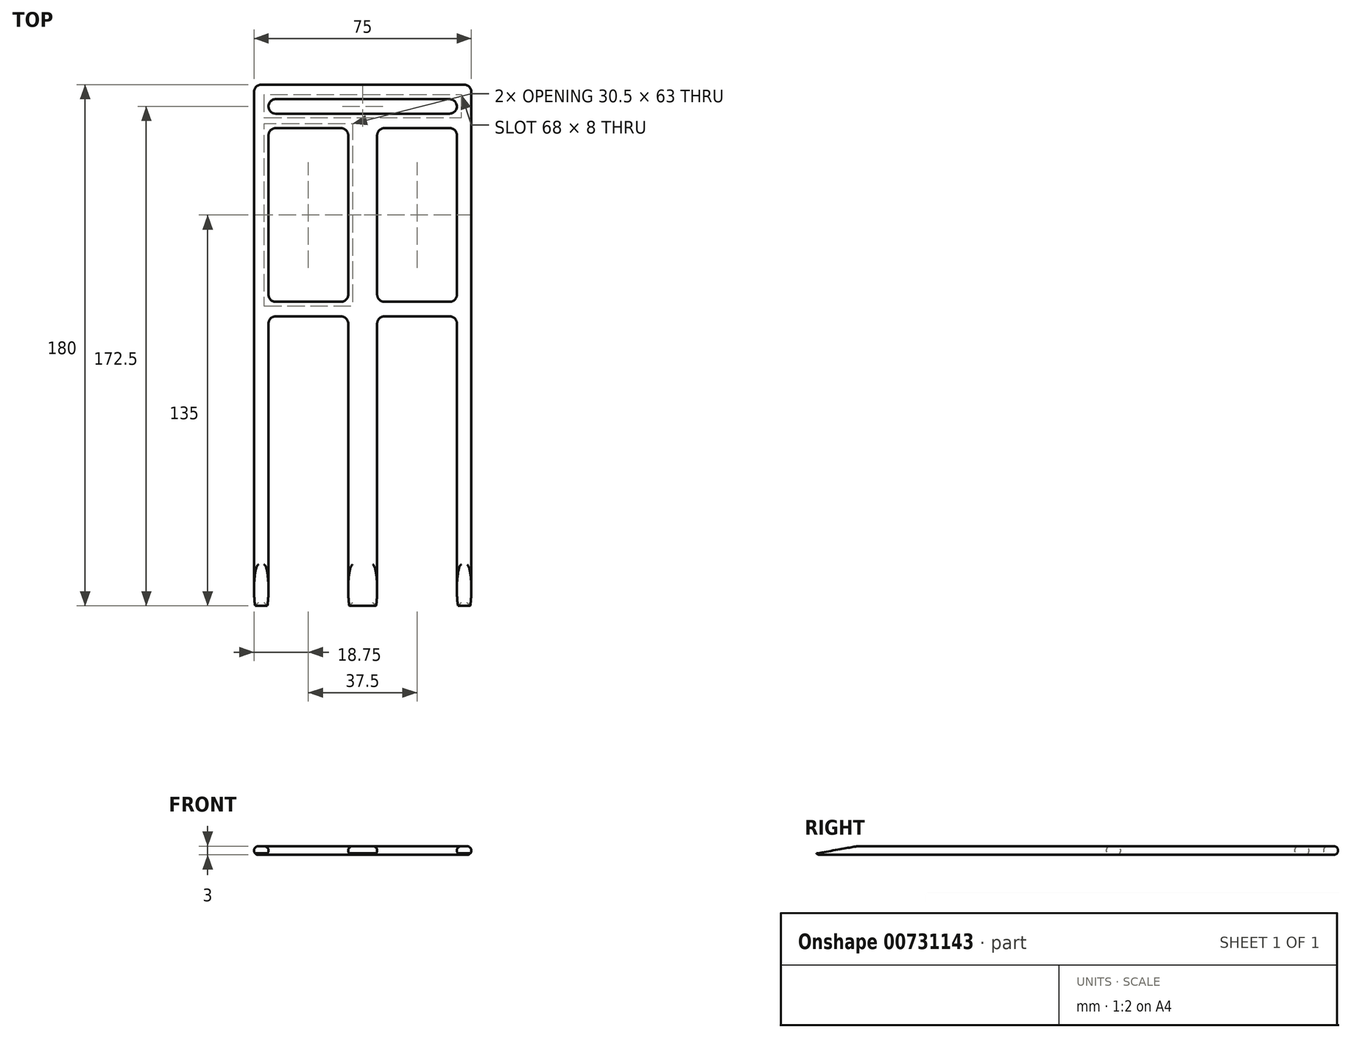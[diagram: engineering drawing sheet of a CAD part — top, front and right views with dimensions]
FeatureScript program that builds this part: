
annotation { "Feature Type Name" : "Feature", "Feature Type Description" : "" }
export const myFeature = defineFeature(function(context is Context, id is Id, definition is map)
    precondition{}
    {
        {
            var Q0;
            Q0=qCreatedBy(makeId("Top.planeOp"),FACE);
            var sketch = newSketch(context, id + "F0", { "sketchPlane" : qUnion([Q0])});
            skLineSegment(sketch, "E0.bottom", {"start": v(35, 90) * mm, "end": v(-35, 90) * mm});
            skLineSegment(sketch, "E0.top", {"start": v(37.5, -90) * mm, "end": v(32.5, -90) * mm});
            skLineSegment(sketch, "E0.left", {"start": v(37.5, 87.5) * mm, "end": v(37.5, -90) * mm});
            skLineSegment(sketch, "E0.right", {"start": v(-37.5, 87.5) * mm, "end": v(-37.5, -90) * mm});
            skPoint(sketch, "E0.middle", {"position": v(0, 0) * mm});
            skLineSegment(sketch, "E1", {"start": v(0, 0) * mm, "end": v(0, -90) * mm, "construction": true});
            skLineSegment(sketch, "E2", {"start": v(0, 0) * mm, "end": v(0, 90) * mm, "construction": true});
            skLineSegment(sketch, "E3", {"start": v(0, -45) * mm, "end": v(-18.75, -45) * mm, "construction": true});
            skLineSegment(sketch, "E4", {"start": v(0, -45) * mm, "end": v(18.75, -45) * mm, "construction": true});
            skLineSegment(sketch, "E5", {"start": v(0, 45) * mm, "end": v(-18.75, 45) * mm, "construction": true});
            skLineSegment(sketch, "E6", {"start": v(0, 45) * mm, "end": v(18.75, 45) * mm, "construction": true});
            skLineSegment(sketch, "E7.bottom", {"start": v(-7.5, 15) * mm, "end": v(-30, 15) * mm});
            skLineSegment(sketch, "E7.top", {"start": v(-7.5, 75) * mm, "end": v(-30, 75) * mm});
            skLineSegment(sketch, "E7.left", {"start": v(-5, 17.5) * mm, "end": v(-5, 72.5) * mm});
            skLineSegment(sketch, "E7.right", {"start": v(-32.5, 17.5) * mm, "end": v(-32.5, 72.5) * mm});
            skPoint(sketch, "E7.middle", {"position": v(-18.75, 45) * mm});
            skLineSegment(sketch, "E8.bottom", {"start": v(30, 15) * mm, "end": v(7.5, 15) * mm});
            skLineSegment(sketch, "E8.top", {"start": v(30, 75) * mm, "end": v(7.5, 75) * mm});
            skLineSegment(sketch, "E8.left", {"start": v(32.5, 17.5) * mm, "end": v(32.5, 72.5) * mm});
            skLineSegment(sketch, "E8.right", {"start": v(5, 17.5) * mm, "end": v(5, 72.5) * mm});
            skPoint(sketch, "E8.middle", {"position": v(18.75, 45) * mm});
            skLineSegment(sketch, "E9.top", {"start": v(-7.5, 10) * mm, "end": v(-30, 10) * mm});
            skLineSegment(sketch, "E9.left", {"start": v(-5, -90) * mm, "end": v(-5, 7.5) * mm});
            skLineSegment(sketch, "E9.right", {"start": v(-32.5, -90) * mm, "end": v(-32.5, 7.5) * mm});
            skPoint(sketch, "E9.middle", {"position": v(-18.75, -45) * mm});
            skLineSegment(sketch, "E10.top", {"start": v(30, 10) * mm, "end": v(7.5, 10) * mm});
            skLineSegment(sketch, "E10.left", {"start": v(32.5, -90) * mm, "end": v(32.5, 7.5) * mm});
            skLineSegment(sketch, "E10.right", {"start": v(5, -90) * mm, "end": v(5, 7.5) * mm});
            skPoint(sketch, "E10.middle", {"position": v(18.75, -45) * mm});
            skLineSegment(sketch, "E11", {"start": v(-18.75, 75) * mm, "end": v(-18.75, 90) * mm, "construction": true});
            skLineSegment(sketch, "E12", {"start": v(18.75, 75) * mm, "end": v(18.75, 90) * mm, "construction": true});
            skLineSegment(sketch, "E13", {"start": v(-18.75, 82.5) * mm, "end": v(18.75, 82.5) * mm, "construction": true});
            skPoint(sketch, "E14", {"position": v(0, 82.5) * mm});
            skLineSegment(sketch, "E15.bottom", {"start": v(30, 80) * mm, "end": v(-30, 80) * mm});
            skLineSegment(sketch, "E15.top", {"start": v(30, 85) * mm, "end": v(-30, 85) * mm});
            skLineSegment(sketch, "E15.left", {"start": v(32.5, 82.5) * mm, "end": v(32.5, 82.5) * mm});
            skLineSegment(sketch, "E15.right", {"start": v(-32.5, 82.5) * mm, "end": v(-32.5, 82.5) * mm});
            skLineSegment(sketch, "E16.trimOffspring", {"start": v(-32.5, -90) * mm, "end": v(-37.5, -90) * mm});
            skPoint(sketch, "E17.orphan", {"position": v(-32.5, -100) * mm});
            skPoint(sketch, "E18.orphan", {"position": v(-5, -100) * mm});
            skLineSegment(sketch, "E19.trimOffspring", {"start": v(5, -90) * mm, "end": v(-5, -90) * mm});
            skPoint(sketch, "E10.bottom.end.orphan", {"position": v(5, -100) * mm});
            skPoint(sketch, "E20.orphan", {"position": v(32.5, -100) * mm});
            skPoint(sketch, "E21.visualSharp", {"position": v(-37.5, 90) * mm});
            skArc(sketch, "E21.filletArc", {"start": v(-35, 90) * mm, "mid": v(-36.77, 89.27) * mm, "end": v(-37.5, 87.5) * mm});
            skPoint(sketch, "E22.visualSharp", {"position": v(37.5, 90) * mm});
            skArc(sketch, "E22.filletArc", {"start": v(37.5, 87.5) * mm, "mid": v(36.77, 89.27) * mm, "end": v(35, 90) * mm});
            skPoint(sketch, "E23.visualSharp", {"position": v(-32.5, 10) * mm});
            skArc(sketch, "E23.filletArc", {"start": v(-30, 10) * mm, "mid": v(-31.77, 9.27) * mm, "end": v(-32.5, 7.5) * mm});
            skPoint(sketch, "E24.visualSharp", {"position": v(-5, 10) * mm});
            skArc(sketch, "E24.filletArc", {"start": v(-5, 7.5) * mm, "mid": v(-5.73, 9.27) * mm, "end": v(-7.5, 10) * mm});
            skPoint(sketch, "E25.visualSharp", {"position": v(5, 10) * mm});
            skArc(sketch, "E25.filletArc", {"start": v(7.5, 10) * mm, "mid": v(5.73, 9.27) * mm, "end": v(5, 7.5) * mm});
            skPoint(sketch, "E26.visualSharp", {"position": v(32.5, 10) * mm});
            skArc(sketch, "E26.filletArc", {"start": v(32.5, 7.5) * mm, "mid": v(31.77, 9.27) * mm, "end": v(30, 10) * mm});
            skPoint(sketch, "E27.visualSharp", {"position": v(32.5, 15) * mm});
            skArc(sketch, "E27.filletArc", {"start": v(30, 15) * mm, "mid": v(31.77, 15.73) * mm, "end": v(32.5, 17.5) * mm});
            skPoint(sketch, "E28.visualSharp", {"position": v(5, 15) * mm});
            skArc(sketch, "E28.filletArc", {"start": v(5, 17.5) * mm, "mid": v(5.73, 15.73) * mm, "end": v(7.5, 15) * mm});
            skPoint(sketch, "E29.visualSharp", {"position": v(-5, 15) * mm});
            skArc(sketch, "E29.filletArc", {"start": v(-7.5, 15) * mm, "mid": v(-5.73, 15.73) * mm, "end": v(-5, 17.5) * mm});
            skPoint(sketch, "E30.visualSharp", {"position": v(-32.5, 15) * mm});
            skArc(sketch, "E30.filletArc", {"start": v(-32.5, 17.5) * mm, "mid": v(-31.77, 15.73) * mm, "end": v(-30, 15) * mm});
            skPoint(sketch, "E31.visualSharp", {"position": v(-32.5, 75) * mm});
            skArc(sketch, "E31.filletArc", {"start": v(-30, 75) * mm, "mid": v(-31.77, 74.27) * mm, "end": v(-32.5, 72.5) * mm});
            skPoint(sketch, "E32.visualSharp", {"position": v(-5, 75) * mm});
            skArc(sketch, "E32.filletArc", {"start": v(-5, 72.5) * mm, "mid": v(-5.73, 74.27) * mm, "end": v(-7.5, 75) * mm});
            skPoint(sketch, "E33.visualSharp", {"position": v(5, 75) * mm});
            skArc(sketch, "E33.filletArc", {"start": v(7.5, 75) * mm, "mid": v(5.73, 74.27) * mm, "end": v(5, 72.5) * mm});
            skPoint(sketch, "E34.visualSharp", {"position": v(32.5, 75) * mm});
            skArc(sketch, "E34.filletArc", {"start": v(32.5, 72.5) * mm, "mid": v(31.77, 74.27) * mm, "end": v(30, 75) * mm});
            skPoint(sketch, "E35.visualSharp", {"position": v(-32.5, 85) * mm});
            skArc(sketch, "E35.filletArc", {"start": v(-30, 85) * mm, "mid": v(-31.77, 84.27) * mm, "end": v(-32.5, 82.5) * mm});
            skPoint(sketch, "E36.visualSharp", {"position": v(-32.5, 80) * mm});
            skArc(sketch, "E36.filletArc", {"start": v(-32.5, 82.5) * mm, "mid": v(-31.77, 80.73) * mm, "end": v(-30, 80) * mm});
            skPoint(sketch, "E37.visualSharp", {"position": v(32.5, 80) * mm});
            skArc(sketch, "E37.filletArc", {"start": v(30, 80) * mm, "mid": v(31.77, 80.73) * mm, "end": v(32.5, 82.5) * mm});
            skPoint(sketch, "E38.visualSharp", {"position": v(32.5, 85) * mm});
            skArc(sketch, "E38.filletArc", {"start": v(32.5, 82.5) * mm, "mid": v(31.77, 84.27) * mm, "end": v(30, 85) * mm});
            skSolve(sketch);
        }
        {
            var Q0;
            Q0 = qSketchRegion(id + "F0", true);
            extrude(context, id + "F1", {"entities" : qUnion([Q0]), "depth" : 3 * mm, "offsetDistance" : 25 * mm});
        }
        {
            var Q0;
            Q0=makeQuery(id+"F1.opExtrude","CAP_EDGE",EDGE,{"disambiguationData":[OSD([sQuery(id+"F0.wireOp",EDGE,"E19.trimOffspring")])],"isStart":false});
            var Q1;
            Q1=makeQuery(id+"F1.opExtrude","CAP_EDGE",EDGE,{"disambiguationData":[OSD([sQuery(id+"F0.wireOp",EDGE,"E0.top")])],"isStart":false});
            var Q2;
            Q2=makeQuery(id+"F1.opExtrude","CAP_EDGE",EDGE,{"disambiguationData":[OSD([sQuery(id+"F0.wireOp",EDGE,"E16.trimOffspring")])],"isStart":false});
            chamfer(context, id + "F2", {"entities" : qUnion([Q0, Q1, Q2]), "chamferType" : ChamferType.OFFSET_ANGLE, "width" : 2.5 * mm, "oppositeDirection" : false, "angle" : 80 * degree});
        }
        {
            var Q0;
            Q0=makeQuery(id+"F1.opExtrude","CAP_FACE",FACE,{"disambiguationData":[OSD([sQuery(id+"F0.wireOp",EDGE,"E0.bottom"),sQuery(id+"F0.wireOp",EDGE,"E0.top"),sQuery(id+"F0.wireOp",EDGE,"E0.left"),sQuery(id+"F0.wireOp",EDGE,"E0.right"),sQuery(id+"F0.wireOp",EDGE,"E7.bottom"),sQuery(id+"F0.wireOp",EDGE,"E7.top"),sQuery(id+"F0.wireOp",EDGE,"E7.left"),sQuery(id+"F0.wireOp",EDGE,"E7.right"),sQuery(id+"F0.wireOp",EDGE,"E8.bottom"),sQuery(id+"F0.wireOp",EDGE,"E8.top"),sQuery(id+"F0.wireOp",EDGE,"E8.left"),sQuery(id+"F0.wireOp",EDGE,"E8.right"),sQuery(id+"F0.wireOp",EDGE,"E9.top"),sQuery(id+"F0.wireOp",EDGE,"E9.left"),sQuery(id+"F0.wireOp",EDGE,"E9.right"),sQuery(id+"F0.wireOp",EDGE,"E10.top"),sQuery(id+"F0.wireOp",EDGE,"E10.left"),sQuery(id+"F0.wireOp",EDGE,"E10.right"),sQuery(id+"F0.wireOp",EDGE,"E15.bottom"),sQuery(id+"F0.wireOp",EDGE,"E15.top"),sQuery(id+"F0.wireOp",EDGE,"E16.trimOffspring"),sQuery(id+"F0.wireOp",EDGE,"E19.trimOffspring"),sQuery(id+"F0.wireOp",EDGE,"E21.filletArc"),sQuery(id+"F0.wireOp",EDGE,"E22.filletArc"),sQuery(id+"F0.wireOp",EDGE,"E23.filletArc"),sQuery(id+"F0.wireOp",EDGE,"E24.filletArc"),sQuery(id+"F0.wireOp",EDGE,"E25.filletArc"),sQuery(id+"F0.wireOp",EDGE,"E26.filletArc"),sQuery(id+"F0.wireOp",EDGE,"E27.filletArc"),sQuery(id+"F0.wireOp",EDGE,"E28.filletArc"),sQuery(id+"F0.wireOp",EDGE,"E29.filletArc"),sQuery(id+"F0.wireOp",EDGE,"E30.filletArc"),sQuery(id+"F0.wireOp",EDGE,"E31.filletArc"),sQuery(id+"F0.wireOp",EDGE,"E32.filletArc"),sQuery(id+"F0.wireOp",EDGE,"E33.filletArc"),sQuery(id+"F0.wireOp",EDGE,"E34.filletArc"),sQuery(id+"F0.wireOp",EDGE,"E35.filletArc"),sQuery(id+"F0.wireOp",EDGE,"E36.filletArc"),sQuery(id+"F0.wireOp",EDGE,"E37.filletArc"),sQuery(id+"F0.wireOp",EDGE,"E38.filletArc")])],"isStart":false});
            var Q1;
            Q1=makeQuery(id+"F1.opExtrude","CAP_FACE",FACE,{"disambiguationData":[OSD([sQuery(id+"F0.wireOp",EDGE,"E0.bottom"),sQuery(id+"F0.wireOp",EDGE,"E0.top"),sQuery(id+"F0.wireOp",EDGE,"E0.left"),sQuery(id+"F0.wireOp",EDGE,"E0.right"),sQuery(id+"F0.wireOp",EDGE,"E7.bottom"),sQuery(id+"F0.wireOp",EDGE,"E7.top"),sQuery(id+"F0.wireOp",EDGE,"E7.left"),sQuery(id+"F0.wireOp",EDGE,"E7.right"),sQuery(id+"F0.wireOp",EDGE,"E8.bottom"),sQuery(id+"F0.wireOp",EDGE,"E8.top"),sQuery(id+"F0.wireOp",EDGE,"E8.left"),sQuery(id+"F0.wireOp",EDGE,"E8.right"),sQuery(id+"F0.wireOp",EDGE,"E9.top"),sQuery(id+"F0.wireOp",EDGE,"E9.left"),sQuery(id+"F0.wireOp",EDGE,"E9.right"),sQuery(id+"F0.wireOp",EDGE,"E10.top"),sQuery(id+"F0.wireOp",EDGE,"E10.left"),sQuery(id+"F0.wireOp",EDGE,"E10.right"),sQuery(id+"F0.wireOp",EDGE,"E15.bottom"),sQuery(id+"F0.wireOp",EDGE,"E15.top"),sQuery(id+"F0.wireOp",EDGE,"E16.trimOffspring"),sQuery(id+"F0.wireOp",EDGE,"E19.trimOffspring"),sQuery(id+"F0.wireOp",EDGE,"E21.filletArc"),sQuery(id+"F0.wireOp",EDGE,"E22.filletArc"),sQuery(id+"F0.wireOp",EDGE,"E23.filletArc"),sQuery(id+"F0.wireOp",EDGE,"E24.filletArc"),sQuery(id+"F0.wireOp",EDGE,"E25.filletArc"),sQuery(id+"F0.wireOp",EDGE,"E26.filletArc"),sQuery(id+"F0.wireOp",EDGE,"E27.filletArc"),sQuery(id+"F0.wireOp",EDGE,"E28.filletArc"),sQuery(id+"F0.wireOp",EDGE,"E29.filletArc"),sQuery(id+"F0.wireOp",EDGE,"E30.filletArc"),sQuery(id+"F0.wireOp",EDGE,"E31.filletArc"),sQuery(id+"F0.wireOp",EDGE,"E32.filletArc"),sQuery(id+"F0.wireOp",EDGE,"E33.filletArc"),sQuery(id+"F0.wireOp",EDGE,"E34.filletArc"),sQuery(id+"F0.wireOp",EDGE,"E35.filletArc"),sQuery(id+"F0.wireOp",EDGE,"E36.filletArc"),sQuery(id+"F0.wireOp",EDGE,"E37.filletArc"),sQuery(id+"F0.wireOp",EDGE,"E38.filletArc")])],"isStart":true});
            fillet(context, id + "F3", {"entities" : qUnion([Q0, Q1]), "radius" : 1.5 * mm, "tangentPropagation" : true, "allowEdgeOverflow" : false});
        }
    });
